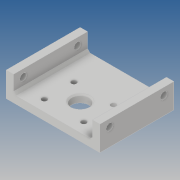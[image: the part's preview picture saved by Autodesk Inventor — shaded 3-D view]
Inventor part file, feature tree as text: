
AUTODESK INVENTOR PART (.ipt)
format: ipt  version: 2019 (Build 230136000, 136)  size: 140,800 bytes
history: native  units: mm
features: other x3, sketch x1, hole x1, extrude x1, chamfer x1
ambient origin geometry x8: Origin, YZ Plane, XZ Plane, XY Plane, X Axis, Y Axis, Z Axis, Center Point
bodies: Solide1 (feature_tree)
feature tree (7):
  other  "base_cloison.ipt"
  sketch  "Esquisse1"
  hole  "Perçage1"  [1 undecoded]
  extrude  "Extrusion1"  Depth=18.0mm
  chamfer  "Chanfrein1"  Distance=40.0mm
  other  "Solide1::base_cloison.ipt"
  other  "FonctionRepérage1"
note: 1 required parameter value undecoded (feature->parameter linkage not recoverable at this tier; creation-order binding heuristic only, values carry confidence <= 0.55)
